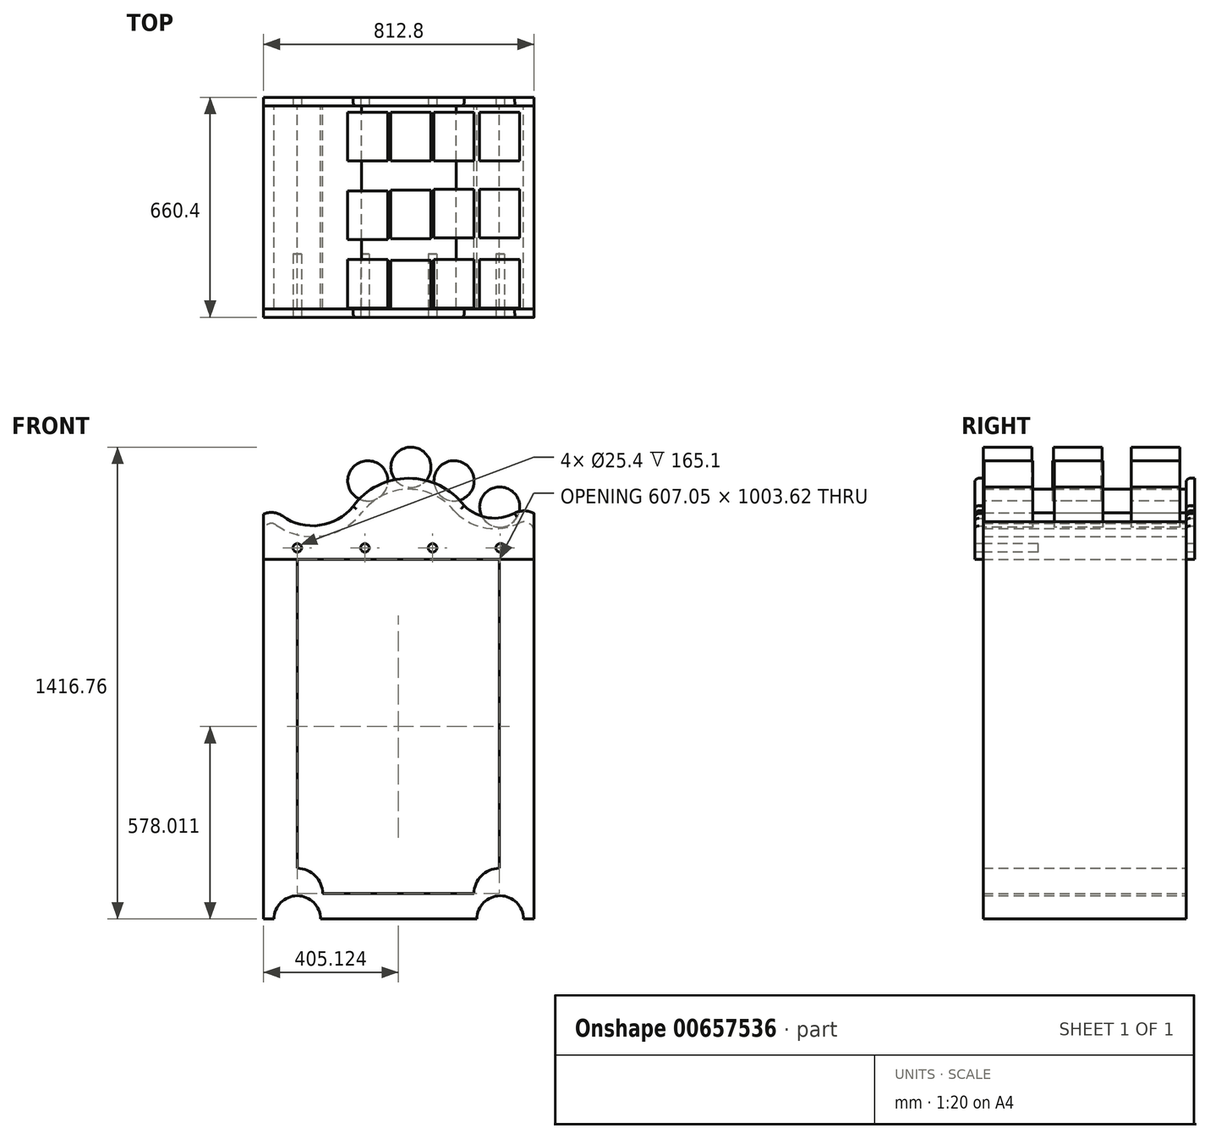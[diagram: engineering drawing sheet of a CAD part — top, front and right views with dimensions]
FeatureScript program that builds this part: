
annotation { "Feature Type Name" : "Feature", "Feature Type Description" : "" }
export const myFeature = defineFeature(function(context is Context, id is Id, definition is map)
    precondition{}
    {
        {
            var Q0;
            Q0=qCreatedBy(makeId("Front.planeOp"),FACE);
            var sketch = newSketch(context, id + "F0", { "sketchPlane" : qUnion([Q0])});
            skLineSegment(sketch, "E0.top", {"start": v(-578.5, -626.49) * mm, "end": v(-546.75, -626.49) * mm});
            skLineSegment(sketch, "E0.left", {"start": v(-578.5, 576.18) * mm, "end": v(-578.5, -626.49) * mm});
            skLineSegment(sketch, "E0.right", {"start": v(234.3, 592.71) * mm, "end": v(234.3, -626.49) * mm});
            skArc(sketch, "E1", {"start": v(-567.62, 580.62) * mm, "mid": v(-422.9, 523.43) * mm, "end": v(-283.57, 592.71) * mm});
            skArc(sketch, "E2", {"start": v(0, 592.71) * mm, "mid": v(-141.79, 663.84) * mm, "end": v(-283.57, 592.71) * mm});
            skArc(sketch, "E3", {"start": v(0, 592.71) * mm, "mid": v(117.15, 545.95) * mm, "end": v(234.3, 592.71) * mm});
            skLineSegment(sketch, "E4", {"start": v(-476.9, 453.33) * mm, "end": v(130.15, 453.33) * mm});
            skPoint(sketch, "E5.visualSharp", {"position": v(-578.5, 592.71) * mm});
            skLineSegment(sketch, "E6", {"start": v(-476.9, -474.09) * mm, "end": v(-476.9, 453.33) * mm});
            skLineSegment(sketch, "E7", {"start": v(130.15, 453.33) * mm, "end": v(130.15, -474.09) * mm});
            skLineSegment(sketch, "E8", {"start": v(-578.5, -626.49) * mm, "end": v(-578.5, -550.29) * mm});
            skLineSegment(sketch, "E9", {"start": v(-400.7, -550.29) * mm, "end": v(53.95, -550.29) * mm});
            skCircle(sketch, "E10", {"center": v(-476.9, -626.49) * mm, "radius": 60.52 * mm});
            skCircle(sketch, "E11", {"center": v(132.7, -626.49) * mm, "radius": 60.52 * mm});
            skArc(sketch, "E12", {"start": v(202.55, -626.49) * mm, "mid": v(132.7, -556.64) * mm, "end": v(62.85, -626.49) * mm});
            skLineSegment(sketch, "E13.trimOffspring", {"start": v(202.55, -626.49) * mm, "end": v(234.3, -626.49) * mm});
            skArc(sketch, "E14", {"start": v(-407.05, -626.49) * mm, "mid": v(-476.9, -556.64) * mm, "end": v(-546.75, -626.49) * mm});
            skLineSegment(sketch, "E15.trimOffspring", {"start": v(-407.05, -626.49) * mm, "end": v(62.85, -626.49) * mm});
            skPoint(sketch, "E16.start.orphan", {"position": v(-578.5, -588.39) * mm});
            skArc(sketch, "E17", {"start": v(-400.7, -550.29) * mm, "mid": v(-423.02, -496.4) * mm, "end": v(-476.9, -474.09) * mm});
            skArc(sketch, "E18", {"start": v(130.15, -474.09) * mm, "mid": v(76.27, -496.4) * mm, "end": v(53.95, -550.29) * mm});
            skLineSegment(sketch, "E19", {"start": v(-578.5, 576.18) * mm, "end": v(-578.5, 592.71) * mm});
            skArc(sketch, "E20", {"start": v(-578.5, 592.71) * mm, "mid": v(-431.04, 521.58) * mm, "end": v(-283.57, 592.71) * mm});
            skSolve(sketch);
        }
        {
            var Q0;
            Q0=makeQuery(id+"F0.imprint","IMPRINT",FACE,{"disambiguationData":[TD([[makeQuery(id+"F0.imprint","IMPRINT",EDGE,{"derivedFrom":sQuery(id+"F0.wireOp",EDGE,"E0.left")}),1.0]])]});
            extrude(context, id + "F1", {"entities" : qUnion([Q0]), "depth" : 609.6 * mm, "offsetDistance" : 25.4 * mm});
        }
        {
            var Q0;
            Q0=makeQuery(id+"F1.opExtrude","SWEPT_EDGE",EDGE,{"disambiguationData":[OSD([sQuery(id+"F0.wireOp",EDGE,"E0.right"),sQuery(id+"F0.wireOp",EDGE,"E3")])]});
            fillet(context, id + "F2", {"entities" : qUnion([Q0]), "radius" : 29.8 * mm, "tangentPropagation" : true, "allowEdgeOverflow" : false});
        }
        {
            var Q0;
            Q0=makeQuery(id+"F1.opExtrude","SWEPT_EDGE",EDGE,{"disambiguationData":[OSD([sQuery(id+"F0.wireOp",EDGE,"E19"),sQuery(id+"F0.wireOp",EDGE,"E20")])]});
            fillet(context, id + "F3", {"entities" : qUnion([Q0]), "radius" : 23.73 * mm, "tangentPropagation" : true, "allowEdgeOverflow" : false});
        }
        {
            var Q0;
            Q0=makeQuery(id+"F1.opExtrude","CAP_FACE",FACE,{"disambiguationData":[OSD([sQuery(id+"F0.wireOp",EDGE,"E0.left"),sQuery(id+"F0.wireOp",EDGE,"E0.right"),sQuery(id+"F0.wireOp",EDGE,"E2"),sQuery(id+"F0.wireOp",EDGE,"E3"),sQuery(id+"F0.wireOp",EDGE,"E4"),sQuery(id+"F0.wireOp",EDGE,"E0.top"),sQuery(id+"F0.wireOp",EDGE,"E6"),sQuery(id+"F0.wireOp",EDGE,"E7"),sQuery(id+"F0.wireOp",EDGE,"E8"),sQuery(id+"F0.wireOp",EDGE,"E9"),sQuery(id+"F0.wireOp",EDGE,"E12"),sQuery(id+"F0.wireOp",EDGE,"E13.trimOffspring"),sQuery(id+"F0.wireOp",EDGE,"E14"),sQuery(id+"F0.wireOp",EDGE,"E15.trimOffspring"),sQuery(id+"F0.wireOp",EDGE,"E17"),sQuery(id+"F0.wireOp",EDGE,"E18"),sQuery(id+"F0.wireOp",EDGE,"E19"),sQuery(id+"F0.wireOp",EDGE,"E20")])],"isStart":false});
            var sketch = newSketch(context, id + "F4", { "sketchPlane" : qUnion([Q0])});
            skLineSegment(sketch, "E21", {"start": v(-476.9, 453.33) * mm, "end": v(-578.5, 453.33) * mm});
            skLineSegment(sketch, "E22", {"start": v(130.15, 453.33) * mm, "end": v(234.3, 453.33) * mm});
            skLineSegment(sketch, "E23", {"start": v(-578.5, 453.33) * mm, "end": v(234.3, 453.33) * mm});
            skArc(sketch, "E24.0", {"start": v(234.3, 591.55) * mm, "mid": v(205.46, 599.06) * mm, "end": v(176.4, 592.43) * mm});
            skArc(sketch, "E24.1", {"start": v(-521.58, 583.7) * mm, "mid": v(-549.3, 594.15) * mm, "end": v(-578.5, 589.21) * mm});
            skArc(sketch, "E24.2", {"start": v(-521.58, 583.7) * mm, "mid": v(-409.81, 555.68) * mm, "end": v(-309.76, 612.83) * mm});
            skArc(sketch, "E24.3", {"start": v(24.99, 614.41) * mm, "mid": v(-142.78, 696.86) * mm, "end": v(-309.76, 612.83) * mm});
            skArc(sketch, "E24.4", {"start": v(24.99, 614.41) * mm, "mid": v(97.08, 578.54) * mm, "end": v(176.4, 592.43) * mm});
            skLineSegment(sketch, "E25", {"start": v(234.3, 453.33) * mm, "end": v(234.3, 591.55) * mm});
            skLineSegment(sketch, "E26", {"start": v(-578.5, 453.33) * mm, "end": v(-578.5, 589.21) * mm});
            skSolve(sketch);
        }
        {
            var Q0;
            {var subQ11=sQuery(id+"F4.wireOp",EDGE,"E24.0");Q0=makeQuery(id+"F4.imprint","IMPRINT",FACE,{"disambiguationData":[TD([[makeQuery(id+"F4.imprint","IMPRINT",EDGE,{"derivedFrom":subQ11}),1.0]])]});}
            var Q1;
            {var subQ7=sQuery(id+"F0.wireOp",EDGE,"E2");Q1=makeQuery(id+"F4.imprint","IMPRINT",FACE,{"disambiguationData":[TD([[makeQuery(id+"F4.imprint","IMPRINT",EDGE,{"derivedFrom":makeQuery(id+"F1.opExtrude","CAP_EDGE",EDGE,{"disambiguationData":[OSD([subQ7])],"isStart":false})}),1.0]])]});}
            extrude(context, id + "F5", {"entities" : qUnion([Q0, Q1]), "depth" : 25.4 * mm, "offsetDistance" : 25.4 * mm});
        }
        {
            var Q0;
            Q0=makeQuery(id+"F5.opExtrude","SWEPT_BODY",BODY,{"disambiguationData":[OSD([sQuery(id+"F4.wireOp",EDGE,"E23"),sQuery(id+"F4.wireOp",EDGE,"E24.0"),sQuery(id+"F4.wireOp",EDGE,"E24.1"),sQuery(id+"F4.wireOp",EDGE,"E24.2"),sQuery(id+"F4.wireOp",EDGE,"E24.3"),sQuery(id+"F4.wireOp",EDGE,"E24.4"),sQuery(id+"F4.wireOp",EDGE,"E25"),sQuery(id+"F4.wireOp",EDGE,"E26")])]});
            transform(context, id + "F6", {"entities" : qUnion([Q0]), "transformType" : TransformType.TRANSLATION_3D, "dx" : 0 * mm, "dy" : 637.54 * mm, "dz" : 0 * mm, "makeCopy" : true});
        }
        {
            var Q0;
            Q0=makeQuery(id+"F6.opPattern","COPY",BODY,{"derivedFrom":makeQuery(id+"F5.opExtrude","SWEPT_BODY",BODY,{"disambiguationData":[OSD([sQuery(id+"F4.wireOp",EDGE,"E23"),sQuery(id+"F4.wireOp",EDGE,"E24.0"),sQuery(id+"F4.wireOp",EDGE,"E24.1"),sQuery(id+"F4.wireOp",EDGE,"E24.2"),sQuery(id+"F4.wireOp",EDGE,"E24.3"),sQuery(id+"F4.wireOp",EDGE,"E24.4"),sQuery(id+"F4.wireOp",EDGE,"E25"),sQuery(id+"F4.wireOp",EDGE,"E26")])]}),"instanceName":"1"});
            deleteBodies(context, id + "F7", {"entities" : qUnion([Q0])});
        }
        {
            var Q0;
            Q0=makeQuery(id+"F5.opExtrude","CAP_FACE",FACE,{"disambiguationData":[OSD([sQuery(id+"F4.wireOp",EDGE,"E23"),sQuery(id+"F4.wireOp",EDGE,"E24.0"),sQuery(id+"F4.wireOp",EDGE,"E24.1"),sQuery(id+"F4.wireOp",EDGE,"E24.2"),sQuery(id+"F4.wireOp",EDGE,"E24.3"),sQuery(id+"F4.wireOp",EDGE,"E24.4"),sQuery(id+"F4.wireOp",EDGE,"E25"),sQuery(id+"F4.wireOp",EDGE,"E26")])],"isStart":false});
            var sketch = newSketch(context, id + "F8", { "sketchPlane" : qUnion([Q0])});
            skLineSegment(sketch, "E27", {"start": v(234.3, 522.44) * mm, "end": v(-578.5, 522.44) * mm});
            skLineSegment(sketch, "E28", {"start": v(-578.5, 522.44) * mm, "end": v(-578.5, 453.33) * mm});
            skLineSegment(sketch, "E29", {"start": v(-578.5, 453.33) * mm, "end": v(-578.5, 487.88) * mm});
            skLineSegment(sketch, "E30", {"start": v(-172.1, 522.44) * mm, "end": v(-172.1, 453.33) * mm});
            skLineSegment(sketch, "E31", {"start": v(-578.5, 522.44) * mm, "end": v(-172.1, 522.44) * mm});
            skLineSegment(sketch, "E32", {"start": v(-172.1, 522.44) * mm, "end": v(234.3, 522.44) * mm});
            skLineSegment(sketch, "E33", {"start": v(31.1, 522.44) * mm, "end": v(31.1, 453.33) * mm});
            skLineSegment(sketch, "E34", {"start": v(-375.3, 522.44) * mm, "end": v(-578.5, 522.44) * mm});
            skLineSegment(sketch, "E35", {"start": v(-476.9, 522.44) * mm, "end": v(-476.9, 500.58) * mm});
            skLineSegment(sketch, "E36", {"start": v(31.1, 522.44) * mm, "end": v(234.3, 522.44) * mm});
            skLineSegment(sketch, "E37", {"start": v(132.7, 522.44) * mm, "end": v(132.7, 500.58) * mm});
            skLineSegment(sketch, "E38", {"start": v(-172.1, 453.33) * mm, "end": v(31.1, 453.33) * mm});
            skLineSegment(sketch, "E39", {"start": v(-172.1, 453.33) * mm, "end": v(-375.3, 453.33) * mm});
            skLineSegment(sketch, "E40", {"start": v(-273.7, 453.33) * mm, "end": v(-273.7, 475.18) * mm});
            skLineSegment(sketch, "E41", {"start": v(-172.1, 522.44) * mm, "end": v(31.1, 522.44) * mm});
            skLineSegment(sketch, "E42", {"start": v(-70.5, 522.44) * mm, "end": v(-70.5, 500.58) * mm});
            skCircle(sketch, "E43", {"center": v(-476.9, 487.88) * mm, "radius": 12.7 * mm});
            skCircle(sketch, "E44", {"center": v(-273.7, 487.88) * mm, "radius": 12.7 * mm});
            skCircle(sketch, "E45", {"center": v(-70.5, 487.88) * mm, "radius": 12.7 * mm});
            skCircle(sketch, "E46", {"center": v(132.7, 487.88) * mm, "radius": 12.7 * mm});
            skPoint(sketch, "E47.orphan", {"position": v(-476.9, 453.33) * mm});
            skLineSegment(sketch, "E48.trimOffspring", {"start": v(-464.2, 487.88) * mm, "end": v(-286.4, 487.88) * mm});
            skLineSegment(sketch, "E49.trimOffspring", {"start": v(-273.7, 500.58) * mm, "end": v(-273.7, 522.44) * mm});
            skLineSegment(sketch, "E50.trimOffspring", {"start": v(-261, 487.88) * mm, "end": v(-83.2, 487.88) * mm});
            skLineSegment(sketch, "E51.trimOffspring", {"start": v(-57.8, 487.88) * mm, "end": v(120, 487.88) * mm});
            skLineSegment(sketch, "E52.trimOffspring", {"start": v(-70.5, 475.18) * mm, "end": v(-70.5, 453.33) * mm});
            skLineSegment(sketch, "E53.trimOffspring", {"start": v(145.4, 487.88) * mm, "end": v(234.3, 487.88) * mm});
            skLineSegment(sketch, "E54.trimOffspring", {"start": v(132.7, 475.18) * mm, "end": v(132.7, 453.33) * mm});
            skSolve(sketch);
        }
        {
            var Q0;
            {var subQ0=sQuery(id+"F8.wireOp",EDGE,"E44");var subQ1=makeQuery(id+"F8.imprint","INTERSECT",VERTEX,{"derivedFrom":[subQ0,sQuery(id+"F8.wireOp",EDGE,"E49.trimOffspring")]});Q0=makeQuery(id+"F8.imprint","IMPRINT",FACE,{"disambiguationData":[TD([[makeQuery(id+"F8.imprint","IMPRINT",EDGE,{"disambiguationData":[TD([[subQ1,1.0]])],"derivedFrom":subQ0}),1.0]])]});}
            var Q1;
            {var subQ0=sQuery(id+"F8.wireOp",EDGE,"E43");var subQ1=makeQuery(id+"F8.imprint","INTERSECT",VERTEX,{"derivedFrom":[sQuery(id+"F8.wireOp",EDGE,"E35"),subQ0]});Q1=makeQuery(id+"F8.imprint","IMPRINT",FACE,{"disambiguationData":[TD([[makeQuery(id+"F8.imprint","IMPRINT",EDGE,{"disambiguationData":[TD([[subQ1,1.0]])],"derivedFrom":subQ0}),1.0]])]});}
            var Q2;
            {var subQ0=sQuery(id+"F8.wireOp",EDGE,"E45");var subQ1=makeQuery(id+"F8.imprint","INTERSECT",VERTEX,{"derivedFrom":[sQuery(id+"F8.wireOp",EDGE,"E42"),subQ0]});Q2=makeQuery(id+"F8.imprint","IMPRINT",FACE,{"disambiguationData":[TD([[makeQuery(id+"F8.imprint","IMPRINT",EDGE,{"disambiguationData":[TD([[subQ1,1.0]])],"derivedFrom":subQ0}),1.0]])]});}
            var Q3;
            {var subQ0=sQuery(id+"F8.wireOp",EDGE,"E46");var subQ1=makeQuery(id+"F8.imprint","INTERSECT",VERTEX,{"derivedFrom":[sQuery(id+"F8.wireOp",EDGE,"E37"),subQ0]});Q3=makeQuery(id+"F8.imprint","IMPRINT",FACE,{"disambiguationData":[TD([[makeQuery(id+"F8.imprint","IMPRINT",EDGE,{"disambiguationData":[TD([[subQ1,1.0]])],"derivedFrom":subQ0}),1.0]])]});}
            extrude(context, id + "F9", {"entities" : qUnion([Q0, Q1, Q2, Q3]), "operationType" : NewBodyOperationType.REMOVE, "oppositeDirection" : true, "depth" : 190.5 * mm, "offsetDistance" : 25.4 * mm});
        }
        {
            var Q0;
            Q0=makeQuery(id+"F5.opExtrude","CAP_EDGE",EDGE,{"disambiguationData":[OSD([sQuery(id+"F4.wireOp",EDGE,"E24.0")])],"isStart":false});
            var Q1;
            Q1=makeQuery(id+"F5.opExtrude","CAP_EDGE",EDGE,{"disambiguationData":[OSD([sQuery(id+"F4.wireOp",EDGE,"E24.4")])],"isStart":false});
            var Q2;
            Q2=makeQuery(id+"F5.opExtrude","CAP_EDGE",EDGE,{"disambiguationData":[OSD([sQuery(id+"F4.wireOp",EDGE,"E24.3")])],"isStart":false});
            var Q3;
            Q3=makeQuery(id+"F5.opExtrude","CAP_EDGE",EDGE,{"disambiguationData":[OSD([sQuery(id+"F4.wireOp",EDGE,"E24.1")])],"isStart":false});
            fillet(context, id + "F10", {"entities" : qUnion([Q0, Q1, Q2, Q3]), "radius" : 12.7 * mm, "tangentPropagation" : true, "allowEdgeOverflow" : false});
        }
        {
            var Q0;
            Q0=makeQuery(id+"F5.opExtrude","SWEPT_BODY",BODY,{"disambiguationData":[OSD([sQuery(id+"F4.wireOp",EDGE,"E23"),sQuery(id+"F4.wireOp",EDGE,"E24.0"),sQuery(id+"F4.wireOp",EDGE,"E24.1"),sQuery(id+"F4.wireOp",EDGE,"E24.2"),sQuery(id+"F4.wireOp",EDGE,"E24.3"),sQuery(id+"F4.wireOp",EDGE,"E24.4"),sQuery(id+"F4.wireOp",EDGE,"E25"),sQuery(id+"F4.wireOp",EDGE,"E26")])]});
            transform(context, id + "F11", {"entities" : qUnion([Q0]), "transformType" : TransformType.TRANSLATION_3D, "dx" : 0 * mm, "dy" : 635 * mm, "dz" : 0 * mm, "makeCopy" : true});
        }
        {
            var Q0;
            Q0=qCreatedBy(makeId("Front.planeOp"),FACE);
            var sketch = newSketch(context, id + "F12", { "sketchPlane" : qUnion([Q0])});
            skCircle(sketch, "E55", {"center": v(-320.83, 115.27) * mm, "radius": 60.33 * mm});
            skSolve(sketch);
        }
        {
            var Q0;
            Q0=makeQuery(id+"F12.imprint","IMPRINT",FACE,{"disambiguationData":[TD([[makeQuery(id+"F12.imprint","IMPRINT",EDGE,{"derivedFrom":sQuery(id+"F12.wireOp",EDGE,"E55")}),1.0]])]});
            extrude(context, id + "F13", {"entities" : qUnion([Q0]), "oppositeDirection" : true, "depth" : 146.05 * mm, "offsetDistance" : 25.4 * mm});
        }
        {
            var Q0;
            Q0=makeQuery(id+"F13.opExtrude","SWEPT_BODY",BODY,{"disambiguationData":[OSD([sQuery(id+"F12.wireOp",EDGE,"E55")])]});
            transform(context, id + "F14", {"entities" : qUnion([Q0]), "transformType" : TransformType.TRANSLATION_3D, "dx" : 452.12 * mm, "dy" : -607.06 * mm, "dz" : 495.3 * mm, "makeCopy" : true});
        }
        {
            var Q0;
            Q0=makeQuery(id+"F14.opPattern","COPY",BODY,{"derivedFrom":makeQuery(id+"F13.opExtrude","SWEPT_BODY",BODY,{"disambiguationData":[OSD([sQuery(id+"F12.wireOp",EDGE,"E55")])]}),"instanceName":"1"});
            transform(context, id + "F15", {"entities" : qUnion([Q0]), "transformType" : TransformType.TRANSLATION_3D, "dx" : 0 * mm, "dy" : 210.82 * mm, "dz" : 0 * mm, "makeCopy" : true});
        }
        {
            var Q0;
            Q0=makeQuery(id+"F15.opPattern","COPY",BODY,{"derivedFrom":makeQuery(id+"F14.opPattern","COPY",BODY,{"derivedFrom":makeQuery(id+"F13.opExtrude","SWEPT_BODY",BODY,{"disambiguationData":[OSD([sQuery(id+"F12.wireOp",EDGE,"E55")])]}),"instanceName":"1"}),"instanceName":"1"});
            transform(context, id + "F16", {"entities" : qUnion([Q0]), "transformType" : TransformType.TRANSLATION_3D, "dx" : 0 * mm, "dy" : 231.14 * mm, "dz" : 0 * mm, "makeCopy" : true});
        }
        {
            var Q0;
            Q0=makeQuery(id+"F13.opExtrude","SWEPT_BODY",BODY,{"disambiguationData":[OSD([sQuery(id+"F12.wireOp",EDGE,"E55")])]});
            deleteBodies(context, id + "F17", {"entities" : qUnion([Q0])});
        }
        {
            var Q0;
            Q0=makeQuery(id+"F14.opPattern","COPY",BODY,{"derivedFrom":makeQuery(id+"F13.opExtrude","SWEPT_BODY",BODY,{"disambiguationData":[OSD([sQuery(id+"F12.wireOp",EDGE,"E55")])]}),"instanceName":"1"});
            transform(context, id + "F18", {"entities" : qUnion([Q0]), "transformType" : TransformType.TRANSLATION_3D, "dx" : -137.16 * mm, "dy" : 0 * mm, "dz" : 78.74 * mm, "makeCopy" : true});
        }
        {
            var Q0;
            Q0=makeQuery(id+"F18.opPattern","COPY",BODY,{"derivedFrom":makeQuery(id+"F14.opPattern","COPY",BODY,{"derivedFrom":makeQuery(id+"F13.opExtrude","SWEPT_BODY",BODY,{"disambiguationData":[OSD([sQuery(id+"F12.wireOp",EDGE,"E55")])]}),"instanceName":"1"}),"instanceName":"1"});
            transform(context, id + "F19", {"entities" : qUnion([Q0]), "transformType" : TransformType.TRANSLATION_3D, "dx" : 0 * mm, "dy" : 210.82 * mm, "dz" : 0 * mm, "makeCopy" : true});
        }
        {
            var Q0;
            Q0=makeQuery(id+"F19.opPattern","COPY",BODY,{"derivedFrom":makeQuery(id+"F18.opPattern","COPY",BODY,{"derivedFrom":makeQuery(id+"F14.opPattern","COPY",BODY,{"derivedFrom":makeQuery(id+"F13.opExtrude","SWEPT_BODY",BODY,{"disambiguationData":[OSD([sQuery(id+"F12.wireOp",EDGE,"E55")])]}),"instanceName":"1"}),"instanceName":"1"}),"instanceName":"1"});
            transform(context, id + "F20", {"entities" : qUnion([Q0]), "transformType" : TransformType.TRANSLATION_3D, "dx" : 0 * mm, "dy" : 231.14 * mm, "dz" : 0 * mm, "makeCopy" : true});
        }
        {
            var Q0;
            Q0=makeQuery(id+"F20.opPattern","COPY",BODY,{"derivedFrom":makeQuery(id+"F19.opPattern","COPY",BODY,{"derivedFrom":makeQuery(id+"F18.opPattern","COPY",BODY,{"derivedFrom":makeQuery(id+"F14.opPattern","COPY",BODY,{"derivedFrom":makeQuery(id+"F13.opExtrude","SWEPT_BODY",BODY,{"disambiguationData":[OSD([sQuery(id+"F12.wireOp",EDGE,"E55")])]}),"instanceName":"1"}),"instanceName":"1"}),"instanceName":"1"}),"instanceName":"1"});
            transform(context, id + "F21", {"entities" : qUnion([Q0]), "transformType" : TransformType.TRANSLATION_3D, "dx" : -259.08 * mm, "dy" : 0 * mm, "dz" : 0 * mm, "makeCopy" : true});
        }
        {
            var Q0;
            Q0=makeQuery(id+"F21.opPattern","COPY",BODY,{"derivedFrom":makeQuery(id+"F20.opPattern","COPY",BODY,{"derivedFrom":makeQuery(id+"F19.opPattern","COPY",BODY,{"derivedFrom":makeQuery(id+"F18.opPattern","COPY",BODY,{"derivedFrom":makeQuery(id+"F14.opPattern","COPY",BODY,{"derivedFrom":makeQuery(id+"F13.opExtrude","SWEPT_BODY",BODY,{"disambiguationData":[OSD([sQuery(id+"F12.wireOp",EDGE,"E55")])]}),"instanceName":"1"}),"instanceName":"1"}),"instanceName":"1"}),"instanceName":"1"}),"instanceName":"1"});
            transform(context, id + "F22", {"entities" : qUnion([Q0]), "transformType" : TransformType.TRANSLATION_3D, "dx" : 0 * mm, "dy" : -236.22 * mm, "dz" : 0 * mm, "makeCopy" : true});
        }
        {
            var Q0;
            Q0=makeQuery(id+"F22.opPattern","COPY",BODY,{"derivedFrom":makeQuery(id+"F21.opPattern","COPY",BODY,{"derivedFrom":makeQuery(id+"F20.opPattern","COPY",BODY,{"derivedFrom":makeQuery(id+"F19.opPattern","COPY",BODY,{"derivedFrom":makeQuery(id+"F18.opPattern","COPY",BODY,{"derivedFrom":makeQuery(id+"F14.opPattern","COPY",BODY,{"derivedFrom":makeQuery(id+"F13.opExtrude","SWEPT_BODY",BODY,{"disambiguationData":[OSD([sQuery(id+"F12.wireOp",EDGE,"E55")])]}),"instanceName":"1"}),"instanceName":"1"}),"instanceName":"1"}),"instanceName":"1"}),"instanceName":"1"}),"instanceName":"1"});
            transform(context, id + "F23", {"entities" : qUnion([Q0]), "transformType" : TransformType.TRANSLATION_3D, "dx" : 0 * mm, "dy" : -205.74 * mm, "dz" : 0 * mm, "makeCopy" : true});
        }
        {
            var Q0;
            Q0=makeQuery(id+"F21.opPattern","COPY",BODY,{"derivedFrom":makeQuery(id+"F20.opPattern","COPY",BODY,{"derivedFrom":makeQuery(id+"F19.opPattern","COPY",BODY,{"derivedFrom":makeQuery(id+"F18.opPattern","COPY",BODY,{"derivedFrom":makeQuery(id+"F14.opPattern","COPY",BODY,{"derivedFrom":makeQuery(id+"F13.opExtrude","SWEPT_BODY",BODY,{"disambiguationData":[OSD([sQuery(id+"F12.wireOp",EDGE,"E55")])]}),"instanceName":"1"}),"instanceName":"1"}),"instanceName":"1"}),"instanceName":"1"}),"instanceName":"1"});
            transform(context, id + "F24", {"entities" : qUnion([Q0]), "transformType" : TransformType.TRANSLATION_3D, "dx" : 129.54 * mm, "dy" : 0 * mm, "dz" : 40.64 * mm, "makeCopy" : true});
        }
        {
            var Q0;
            Q0=makeQuery(id+"F24.opPattern","COPY",BODY,{"derivedFrom":makeQuery(id+"F21.opPattern","COPY",BODY,{"derivedFrom":makeQuery(id+"F20.opPattern","COPY",BODY,{"derivedFrom":makeQuery(id+"F19.opPattern","COPY",BODY,{"derivedFrom":makeQuery(id+"F18.opPattern","COPY",BODY,{"derivedFrom":makeQuery(id+"F14.opPattern","COPY",BODY,{"derivedFrom":makeQuery(id+"F13.opExtrude","SWEPT_BODY",BODY,{"disambiguationData":[OSD([sQuery(id+"F12.wireOp",EDGE,"E55")])]}),"instanceName":"1"}),"instanceName":"1"}),"instanceName":"1"}),"instanceName":"1"}),"instanceName":"1"}),"instanceName":"1"});
            transform(context, id + "F25", {"entities" : qUnion([Q0]), "transformType" : TransformType.TRANSLATION_3D, "dx" : 0 * mm, "dy" : -233.68 * mm, "dz" : 0 * mm, "makeCopy" : true});
        }
        {
            var Q0;
            Q0=makeQuery(id+"F25.opPattern","COPY",BODY,{"derivedFrom":makeQuery(id+"F24.opPattern","COPY",BODY,{"derivedFrom":makeQuery(id+"F21.opPattern","COPY",BODY,{"derivedFrom":makeQuery(id+"F20.opPattern","COPY",BODY,{"derivedFrom":makeQuery(id+"F19.opPattern","COPY",BODY,{"derivedFrom":makeQuery(id+"F18.opPattern","COPY",BODY,{"derivedFrom":makeQuery(id+"F14.opPattern","COPY",BODY,{"derivedFrom":makeQuery(id+"F13.opExtrude","SWEPT_BODY",BODY,{"disambiguationData":[OSD([sQuery(id+"F12.wireOp",EDGE,"E55")])]}),"instanceName":"1"}),"instanceName":"1"}),"instanceName":"1"}),"instanceName":"1"}),"instanceName":"1"}),"instanceName":"1"}),"instanceName":"1"});
            transform(context, id + "F26", {"entities" : qUnion([Q0]), "transformType" : TransformType.TRANSLATION_3D, "dx" : 0 * mm, "dy" : -210.82 * mm, "dz" : 0 * mm, "makeCopy" : true});
        }
    });
